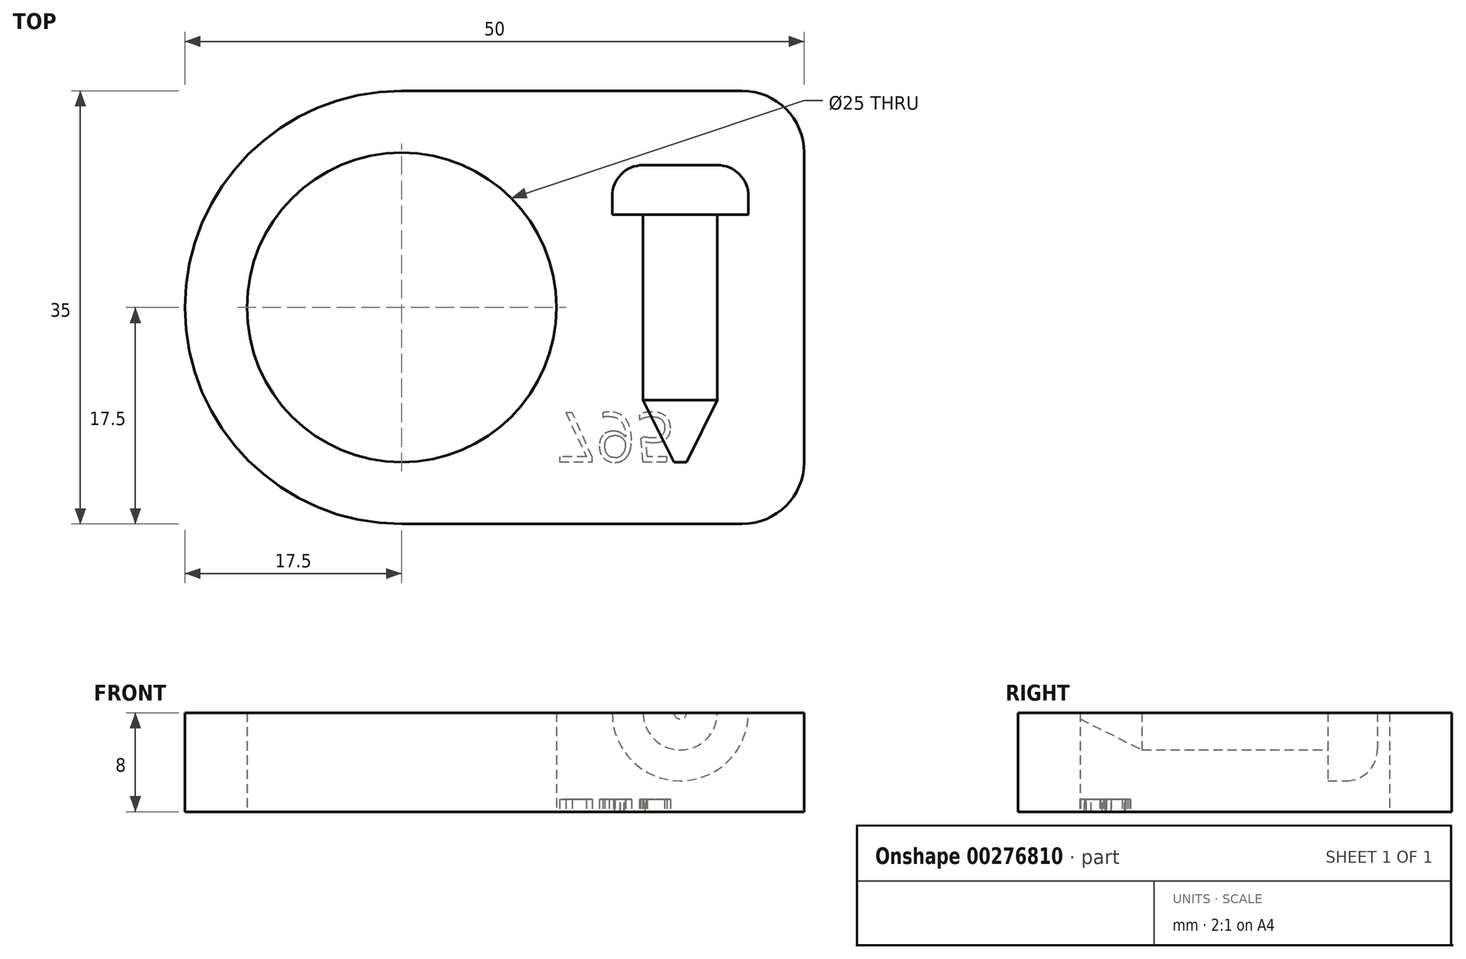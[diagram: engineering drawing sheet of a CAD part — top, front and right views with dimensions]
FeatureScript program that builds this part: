
annotation { "Feature Type Name" : "Feature", "Feature Type Description" : "" }
export const myFeature = defineFeature(function(context is Context, id is Id, definition is map)
    precondition{}
    {
        {
            var Q0;
            Q0=qCreatedBy(makeId("Top.planeOp"),FACE);
            var sketch = newSketch(context, id + "F0", { "sketchPlane" : qUnion([Q0])});
            skLineSegment(sketch, "E0.bottom", {"start": v(17.5, 0) * mm, "end": v(45, 0) * mm});
            skLineSegment(sketch, "E0.top", {"start": v(17.5, 35) * mm, "end": v(45, 35) * mm});
            skLineSegment(sketch, "E0.left", {"start": v(0, 17.5) * mm, "end": v(0, 17.5) * mm});
            skLineSegment(sketch, "E0.right", {"start": v(50, 5) * mm, "end": v(50, 30) * mm});
            skLineSegment(sketch, "E1.bottom", {"start": v(0, 0) * mm, "end": v(17.5, 0) * mm, "construction": true});
            skLineSegment(sketch, "E1.top", {"start": v(0, 17.5) * mm, "end": v(17.5, 17.5) * mm, "construction": true});
            skLineSegment(sketch, "E1.left", {"start": v(0, 0) * mm, "end": v(0, 17.5) * mm, "construction": true});
            skLineSegment(sketch, "E1.right", {"start": v(17.5, 0) * mm, "end": v(17.5, 17.5) * mm, "construction": true});
            skCircle(sketch, "E2", {"center": v(17.5, 17.5) * mm, "radius": 12.5 * mm});
            skPoint(sketch, "E3.visualSharp", {"position": v(0, 0) * mm});
            skArc(sketch, "E3.filletArc", {"start": v(0, 17.5) * mm, "mid": v(5.13, 5.13) * mm, "end": v(17.5, 0) * mm});
            skPoint(sketch, "E4.visualSharp", {"position": v(0, 35) * mm});
            skArc(sketch, "E4.filletArc", {"start": v(17.5, 35) * mm, "mid": v(5.13, 29.87) * mm, "end": v(0, 17.5) * mm});
            skPoint(sketch, "E5.visualSharp", {"position": v(50, 35) * mm});
            skArc(sketch, "E5.filletArc", {"start": v(50, 30) * mm, "mid": v(48.54, 33.54) * mm, "end": v(45, 35) * mm});
            skPoint(sketch, "E6.visualSharp", {"position": v(50, 0) * mm});
            skArc(sketch, "E6.filletArc", {"start": v(45, 0) * mm, "mid": v(48.54, 1.46) * mm, "end": v(50, 5) * mm});
            skSolve(sketch);
        }
        {
            var Q0;
            Q0=makeQuery(id+"F0.imprint","IMPRINT",FACE,{"disambiguationData":[TD([[makeQuery(id+"F0.imprint","IMPRINT",EDGE,{"derivedFrom":sQuery(id+"F0.wireOp",EDGE,"E0.bottom")}),1.0]])]});
            extrude(context, id + "F1", {"entities" : qUnion([Q0]), "depth" : 8 * mm});
        }
        {
            var Q0;
            Q0=makeQuery(id+"F1.opExtrude","CAP_FACE",FACE,{"disambiguationData":[OSD([sQuery(id+"F0.wireOp",EDGE,"E0.bottom"),sQuery(id+"F0.wireOp",EDGE,"E0.top"),sQuery(id+"F0.wireOp",EDGE,"E0.right"),sQuery(id+"F0.wireOp",EDGE,"E2"),sQuery(id+"F0.wireOp",EDGE,"E3.filletArc"),sQuery(id+"F0.wireOp",EDGE,"E4.filletArc"),sQuery(id+"F0.wireOp",EDGE,"E5.filletArc"),sQuery(id+"F0.wireOp",EDGE,"E6.filletArc")])],"isStart":false});
            var sketch = newSketch(context, id + "F2", { "sketchPlane" : qUnion([Q0])});
            skLineSegment(sketch, "E7.bottom", {"start": v(0, 0) * mm, "end": v(40, 0) * mm, "construction": true});
            skLineSegment(sketch, "E7.top", {"start": v(0, 5) * mm, "end": v(40, 5) * mm, "construction": true});
            skLineSegment(sketch, "E7.left", {"start": v(0, 0) * mm, "end": v(0, 5) * mm, "construction": true});
            skLineSegment(sketch, "E7.right", {"start": v(40, 0) * mm, "end": v(40, 5) * mm, "construction": true});
            skLineSegment(sketch, "E8.left", {"start": v(40, 5) * mm, "end": v(40, 25) * mm});
            skLineSegment(sketch, "E9.bottom", {"start": v(43, 25) * mm, "end": v(45.5, 25) * mm});
            skLineSegment(sketch, "E9.top", {"start": v(40, 29) * mm, "end": v(43, 29) * mm});
            skLineSegment(sketch, "E9.left", {"start": v(40, 25) * mm, "end": v(40, 29) * mm});
            skLineSegment(sketch, "E9.right", {"start": v(45.5, 25) * mm, "end": v(45.5, 26.5) * mm});
            skLineSegment(sketch, "E10", {"start": v(40, 5) * mm, "end": v(40.5, 5) * mm});
            skLineSegment(sketch, "E11", {"start": v(43, 25) * mm, "end": v(43, 10) * mm});
            skLineSegment(sketch, "E12", {"start": v(43, 10) * mm, "end": v(40.5, 5) * mm});
            skPoint(sketch, "E13.visualSharp", {"position": v(45.5, 29) * mm});
            skArc(sketch, "E13.filletArc", {"start": v(45.5, 26.5) * mm, "mid": v(44.77, 28.27) * mm, "end": v(43, 29) * mm});
            skSolve(sketch);
        }
        {
            var Q0;
            Q0=makeQuery(id+"F2.imprint","IMPRINT",FACE,{"disambiguationData":[TD([[makeQuery(id+"F2.imprint","IMPRINT",EDGE,{"derivedFrom":sQuery(id+"F2.wireOp",EDGE,"E8.left")}),-1.0]])]});
            var Q1;
            Q1=sQuery(id+"F2.wireOp",EDGE,"E8.left");
            revolve(context, id + "F3", {"operationType" : NewBodyOperationType.REMOVE, "entities" : qUnion([Q0]), "axis" : qUnion([Q1]), "revolveType" : RevolveType.FULL, "oppositeDirection" : true});
        }
        {
            var Q0;
            Q0=makeQuery(id+"F1.opExtrude","CAP_FACE",FACE,{"disambiguationData":[OSD([sQuery(id+"F0.wireOp",EDGE,"E0.bottom"),sQuery(id+"F0.wireOp",EDGE,"E0.top"),sQuery(id+"F0.wireOp",EDGE,"E0.right"),sQuery(id+"F0.wireOp",EDGE,"E2"),sQuery(id+"F0.wireOp",EDGE,"E3.filletArc"),sQuery(id+"F0.wireOp",EDGE,"E4.filletArc"),sQuery(id+"F0.wireOp",EDGE,"E5.filletArc"),sQuery(id+"F0.wireOp",EDGE,"E6.filletArc")])],"isStart":true});
            var sketch = newSketch(context, id + "F4", { "sketchPlane" : qUnion([Q0])});
            skLineSegment(sketch, "E14.bottom", {"start": v(0, 0) * mm, "end": v(30, 0) * mm, "construction": true});
            skLineSegment(sketch, "E14.top", {"start": v(0, -5) * mm, "end": v(17.5, -5) * mm, "construction": true});
            skLineSegment(sketch, "E14.left", {"start": v(0, 0) * mm, "end": v(0, -5) * mm, "construction": true});
            skLineSegment(sketch, "E15", {"start": v(30, 0) * mm, "end": v(30, -5) * mm, "construction": true});
            skText(sketch, "E16", { "text": "795", "fontName": "OpenSans-Regular.ttf"});
            const initialGuessF4  = {"E16": [0.03, -0.009, 1, 0, 0.004]};
            skSetInitialGuess(sketch, initialGuessF4);
            skSolve(sketch);
        }
        {
            var Q0;
            Q0 = qSketchRegion(id + "F4", true);
            extrude(context, id + "F5", {"entities" : qUnion([Q0]), "operationType" : NewBodyOperationType.REMOVE, "oppositeDirection" : true, "depth" : 1 * mm});
        }
    });
